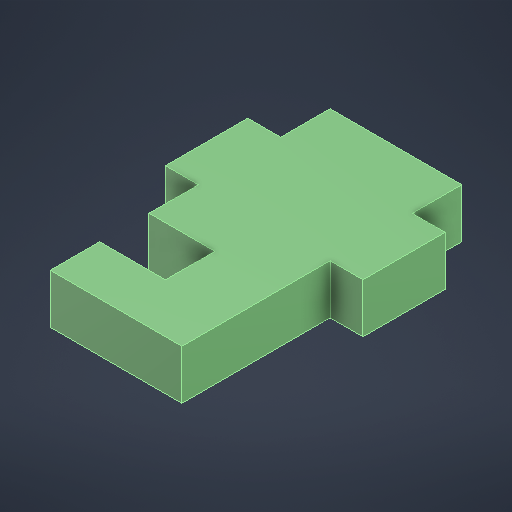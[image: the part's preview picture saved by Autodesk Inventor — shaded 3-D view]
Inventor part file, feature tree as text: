
AUTODESK INVENTOR PART (.ipt)
format: ipt  version: 2025.3 (Build 293356030, 356C)  size: 222,720 bytes
history: native  units: mm
features: other x1, extrude x1, sketch x1
ambient origin geometry x8: Origin, YZ Plane, XZ Plane, XY Plane, X Axis, Y Axis, Z Axis, Center Point
bodies: Body1 (feature_tree)
feature tree (3):
  other  "實體1"
  extrude  "擠出1"  Depth=8.0mm
  sketch  "草圖1"
